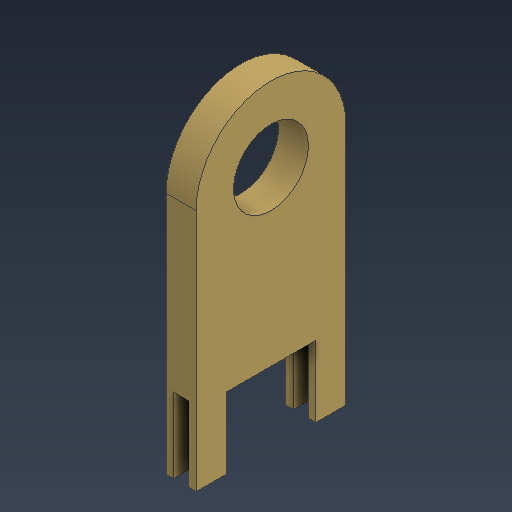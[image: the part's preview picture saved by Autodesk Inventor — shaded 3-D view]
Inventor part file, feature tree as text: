
AUTODESK INVENTOR PART (.ipt)
format: ipt  version: 2021 (Build 250183000, 183)  size: 161,280 bytes
history: native  units: mm
features: extrude x4, sketch x4, other x2, fillet x1
ambient origin geometry x8: Origin, YZ Plane, XZ Plane, XY Plane, X Axis, Y Axis, Z Axis, Center Point
bodies: Body1 (feature_tree)
feature tree (11):
  other  "Terminais"
  other  "Sólido1"
  extrude  "Extrusão1"  Depth=2.0mm
  extrude  "Extrusão2"  Depth=1.0mm
  fillet  "Arredondamento1"  Radius=1.0mm
  extrude  "Extrusão3"  Depth=1.0mm
  extrude  "Extrusão4"  Depth=0.95mm TaperAngle=0.0deg
  sketch  "Esboço1"  dims[d0=0.4mm d1=2.0mm]
  sketch  "Esboço2"  dims[d2=4.25mm d3=0.0mm d4=1.0mm d5=1.0mm]
  sketch  "Esboço3"  dims[d6=4.25mm d7=0.0mm d8=1.0mm]
  sketch  "Esboço4"  dims[d9=1.2mm d10=0.95mm d11=0.0mm d12=0.2mm d13=1.0mm d14=0.0mm d15=0.1mm]
